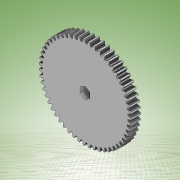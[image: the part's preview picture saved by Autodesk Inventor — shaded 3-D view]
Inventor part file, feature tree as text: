
AUTODESK INVENTOR PART (.ipt)
format: ipt  version: 2022 (Build 260153000, 153)  size: 2,803,200 bytes
history: native  units: mm
features: other x1, extrude x1, sketch x1
ambient origin geometry x8: Origin, YZ Plane, XZ Plane, XY Plane, X Axis, Y Axis, Z Axis, Center Point
bodies: Body1 (feature_tree)
feature tree (3):
  other  "Sólido1"
  extrude  "Extrusión1"  Depth=6.0mm TaperAngle=0.0deg
  sketch  "Boceto1"  dims[d0=6.0mm d1=6.0mm d2=0.0mm]
